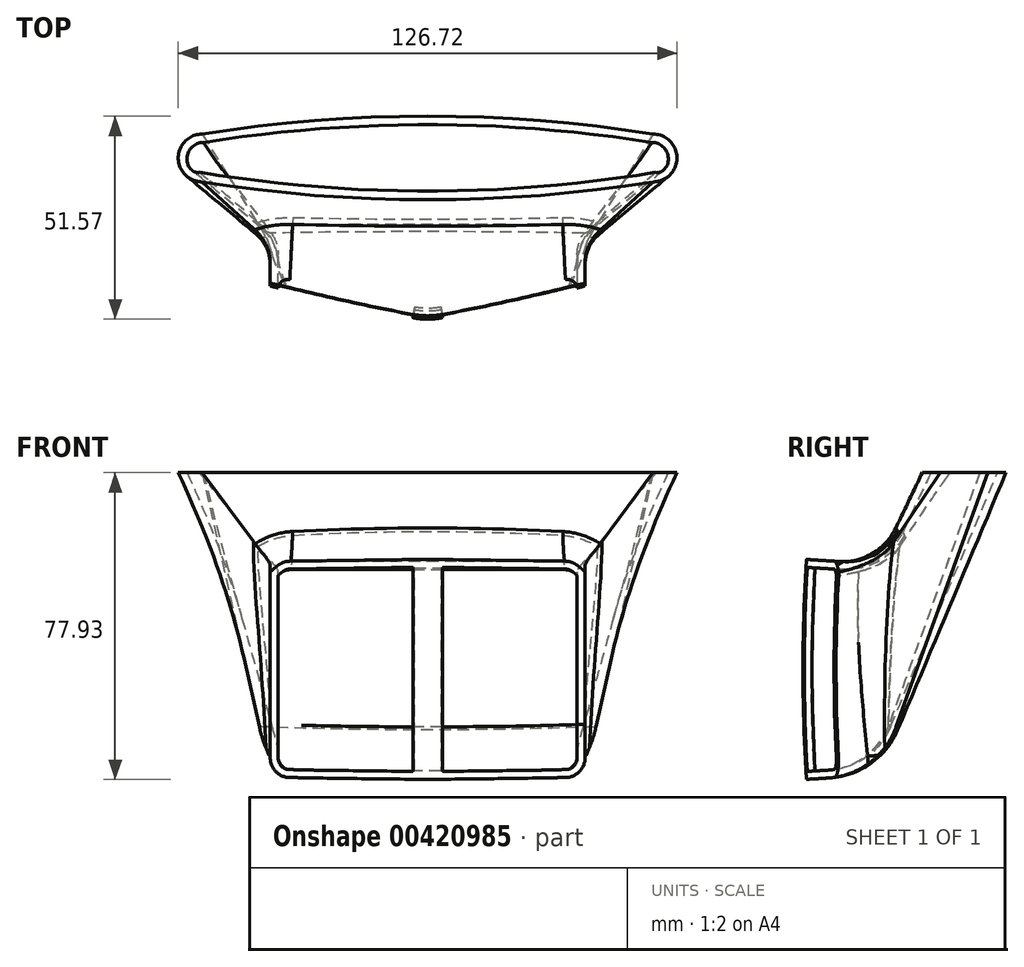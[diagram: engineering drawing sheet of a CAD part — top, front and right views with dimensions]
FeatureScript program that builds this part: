
annotation { "Feature Type Name" : "Feature", "Feature Type Description" : "" }
export const myFeature = defineFeature(function(context is Context, id is Id, definition is map)
    precondition{}
    {
        {
            var Q0;
            Q0=qCreatedBy(makeId("Top.planeOp"),FACE);
            var sketch = newSketch(context, id + "F0", { "sketchPlane" : qUnion([Q0])});
            skArc(sketch, "E0", {"start": v(-40, 0.85) * mm, "mid": v(-20.07, -3.87) * mm, "end": v(0, -7.9) * mm});
            skPoint(sketch, "E1.orphan", {"position": v(0, -7.9) * mm});
            skPoint(sketch, "E2.bottom.start.orphan", {"position": v(36.6, 0) * mm});
            skLineSegment(sketch, "E3", {"start": v(0, -7.9) * mm, "end": v(0, -4.86) * mm});
            skLineSegment(sketch, "E4.MirrorCS", {"start": v(-40, 0.85) * mm, "end": v(-40, 10.85) * mm});
            skPoint(sketch, "E5.orphan", {"position": v(40, -7.9) * mm});
            skPoint(sketch, "E6.orphan", {"position": v(74.82, 26.5) * mm});
            skPoint(sketch, "E7.orphan", {"position": v(-40, -7.9) * mm});
            skPoint(sketch, "E2.left.start.orphan", {"position": v(-36.6, 0) * mm});
            skPoint(sketch, "E8.orphan", {"position": v(-74.82, 26.5) * mm});
            skLineSegment(sketch, "E9", {"start": v(57.25, 582.23) * mm, "end": v(108.33, 582.23) * mm});
            skLineSegment(sketch, "E10.0", {"start": v(-40, 10.85) * mm, "end": v(0, 10.85) * mm});
            skPoint(sketch, "E11.orphan", {"position": v(40, 26.5) * mm});
            skPoint(sketch, "E12.0.end.orphan", {"position": v(0, 26.5) * mm});
            skPoint(sketch, "E13.orphan", {"position": v(-40, 26.5) * mm});
            skLineSegment(sketch, "E14", {"start": v(0, -4.86) * mm, "end": v(0, 10.85) * mm});
            skPoint(sketch, "E15.0.end.orphan", {"position": v(40, 10.85) * mm});
            skLineSegment(sketch, "E16.MirrorCS", {"start": v(40, 10.85) * mm, "end": v(0, 10.85) * mm});
            skLineSegment(sketch, "E17.MirrorCS", {"start": v(40, 0.85) * mm, "end": v(40, 10.85) * mm});
            skArc(sketch, "E18.MirrorCS", {"start": v(40, 0.85) * mm, "mid": v(20.07, -3.87) * mm, "end": v(0, -7.9) * mm});
            skSolve(sketch);
        }
        {
            var Q0;
            Q0=qCreatedBy(makeId("Top.planeOp"),FACE);
            var sketch = newSketch(context, id + "F1", { "sketchPlane" : qUnion([Q0])});
            skLineSegment(sketch, "E19", {"start": v(-37.76, 450) * mm, "end": v(36.32, 450) * mm});
            skSolve(sketch);
        }
        {
            var Q0;
            Q0=makeQuery(id+"F0.imprint","IMPRINT",FACE,{"disambiguationData":[TD([[makeQuery(id+"F0.imprint","IMPRINT",EDGE,{"derivedFrom":sQuery(id+"F0.wireOp",EDGE,"E3")}),-1.0]])]});
            var Q1;
            Q1=makeQuery(id+"F0.imprint","IMPRINT",FACE,{"disambiguationData":[TD([[makeQuery(id+"F0.imprint","IMPRINT",EDGE,{"derivedFrom":sQuery(id+"F0.wireOp",EDGE,"E0")}),1.0]])]});
            var Q2;
            Q2=sQuery(id+"F1.wireOp",EDGE,"E19");
            revolve(context, id + "F2", {"surfaceOperationType" : NewSurfaceOperationType.NEW, "entities" : qUnion([Q0, Q1]), "axis" : qUnion([Q2]), "revolveType" : RevolveType.SYMMETRIC, "angle" : 7 * degree});
        }
        {
            var Q0;
            Q0=makeQuery(id+"F2.opRevolve","SWEPT_EDGE",EDGE,{"disambiguationData":[OSD([sQuery(id+"F0.wireOp",EDGE,"E0"),sQuery(id+"F0.wireOp",EDGE,"E3"),sQuery(id+"F0.wireOp",EDGE,"E18.MirrorCS")])]});
            fillet(context, id + "F3", {"entities" : qUnion([Q0]), "radius" : 20 * mm, "tangentPropagation" : true, "allowEdgeOverflow" : false});
        }
        {
            var Q0;
            Q0=qCreatedBy(makeId("Top.planeOp"),FACE);
            cPlane(context, id + "F4", {"entities" : qUnion([Q0]), "cplaneType" : CPlaneType.OFFSET, "offset" : 50 * mm, "width" : 150 * mm, "height" : 150 * mm});
        }
        {
            var Q0;
            Q0=qCreatedBy(id+"F4.planeOp",FACE);
            var sketch = newSketch(context, id + "F5", { "sketchPlane" : qUnion([Q0])});
            skLineSegment(sketch, "E20.left", {"start": v(0, 27.31) * mm, "end": v(0, 27.31) * mm});
            skLineSegment(sketch, "E20.right", {"start": v(-57.28, 27.31) * mm, "end": v(-57.28, 27.31) * mm});
            skLineSegment(sketch, "E21.top", {"start": v(-57.28, 39.46) * mm, "end": v(-57.28, 39.46) * mm});
            skArc(sketch, "E22", {"start": v(57.28, 27.31) * mm, "mid": v(63.36, 33.38) * mm, "end": v(57.28, 39.46) * mm});
            skPoint(sketch, "E23.MirrorCS.end.orphan", {"position": v(57.28, 39.46) * mm});
            skArc(sketch, "E24.MirrorCS", {"start": v(-57.28, 27.31) * mm, "mid": v(-63.36, 33.38) * mm, "end": v(-57.28, 39.46) * mm});
            skPoint(sketch, "E25.MirrorCS.start.orphan", {"position": v(0, 27.31) * mm});
            skPoint(sketch, "E26.end.orphan", {"position": v(57.28, 27.31) * mm});
            skArc(sketch, "E27", {"start": v(57.28, 39.46) * mm, "mid": v(0, 44.01) * mm, "end": v(-57.28, 39.46) * mm});
            skPoint(sketch, "E28.MirrorCS.end.orphan", {"position": v(0, 39.46) * mm});
            skArc(sketch, "E29.MirrorCS", {"start": v(57.28, 27.31) * mm, "mid": v(0, 22.75) * mm, "end": v(-57.28, 27.31) * mm});
            skSolve(sketch);
        }
        {
            var Q1;
            Q1=makeQuery(id+"F5.imprint","IMPRINT",FACE,{"disambiguationData":[TD([[makeQuery(id+"F5.imprint","IMPRINT",EDGE,{"derivedFrom":sQuery(id+"F5.wireOp",EDGE,"E22")}),1.0]])]});
            var Q2;
            Q2=makeQuery(id+"F2.opRevolve","SWEPT_FACE",FACE,{"disambiguationData":[OSD([sQuery(id+"F0.wireOp",EDGE,"E10.0"),sQuery(id+"F0.wireOp",EDGE,"E16.MirrorCS")])]});
            loft(context, id + "F6", {"operationType" : NewBodyOperationType.ADD, "sheetProfilesArray" : [{ "sheetProfileEntities" : qUnion([Q1]) }, { "sheetProfileEntities" : qUnion([Q2]) }]});
        }
        {
            var Q0;
            {var subQ0=sQuery(id+"F0.wireOp",EDGE,"E17.MirrorCS");var subQ1=sQuery(id+"F0.wireOp",EDGE,"E16.MirrorCS");Q0=makeQuery(id+"F6.boolean.opBoolean","MERGE",EDGE,{"derivedFrom":[makeQuery(id+"F2.opRevolve","SWEPT_EDGE",EDGE,{"disambiguationData":[OSD([subQ1,subQ0])]}),makeQuery(id+"F6.opLoft","MID_CAP_EDGE",EDGE,{"disambiguationData":[OSD([subQ1,subQ0])],"capPos":1.0})]});}
            var Q1;
            {var subQ0=sQuery(id+"F0.wireOp",EDGE,"E10.0");var subQ1=sQuery(id+"F0.wireOp",EDGE,"E4.MirrorCS");Q1=makeQuery(id+"F6.boolean.opBoolean","MERGE",EDGE,{"derivedFrom":[makeQuery(id+"F2.opRevolve","SWEPT_EDGE",EDGE,{"disambiguationData":[OSD([subQ1,subQ0])]}),makeQuery(id+"F6.opLoft","MID_CAP_EDGE",EDGE,{"disambiguationData":[OSD([subQ1,subQ0])],"capPos":1.0})]});}
            fillet(context, id + "F7", {"entities" : qUnion([Q0, Q1]), "radius" : 10 * mm, "tangentPropagation" : true, "allowEdgeOverflow" : false});
        }
        {
            var Q0;
            {var subQ0=sQuery(id+"F0.wireOp",EDGE,"E17.MirrorCS");var subQ1=sQuery(id+"F0.wireOp",EDGE,"E16.MirrorCS");Q0=makeQuery(id+"F7.opFillet","BLEND_EDGE",EDGE,{"blendedFrom":[makeQuery(id+"F6.boolean.opBoolean","MERGE",EDGE,{"derivedFrom":[makeQuery(id+"F2.opRevolve","SWEPT_EDGE",EDGE,{"disambiguationData":[OSD([subQ1,subQ0])]}),makeQuery(id+"F6.opLoft","MID_CAP_EDGE",EDGE,{"disambiguationData":[OSD([subQ1,subQ0])],"capPos":1.0})]}),makeQuery(id+"F2.opRevolve","CAP_FACE",FACE,{"disambiguationData":[OSD([sQuery(id+"F0.wireOp",EDGE,"E0"),sQuery(id+"F0.wireOp",EDGE,"E4.MirrorCS"),sQuery(id+"F0.wireOp",EDGE,"E10.0"),subQ1,subQ0,sQuery(id+"F0.wireOp",EDGE,"E18.MirrorCS")])],"isStart":true})],"blendedInto":[makeQuery(id+"F2.opRevolve","CAP_FACE",FACE,{"disambiguationData":[OSD([sQuery(id+"F0.wireOp",EDGE,"E0"),sQuery(id+"F0.wireOp",EDGE,"E4.MirrorCS"),sQuery(id+"F0.wireOp",EDGE,"E10.0"),subQ1,subQ0,sQuery(id+"F0.wireOp",EDGE,"E18.MirrorCS")])],"isStart":true})]});}
            var Q1;
            Q1=makeQuery(id+"F2.opRevolve","CAP_EDGE",EDGE,{"disambiguationData":[OSD([sQuery(id+"F0.wireOp",EDGE,"E4.MirrorCS")])],"isStart":true});
            var Q2;
            Q2=makeQuery(id+"F2.opRevolve","CAP_EDGE",EDGE,{"disambiguationData":[OSD([sQuery(id+"F0.wireOp",EDGE,"E4.MirrorCS")])],"isStart":false});
            var Q3;
            Q3=makeQuery(id+"F2.opRevolve","CAP_EDGE",EDGE,{"disambiguationData":[OSD([sQuery(id+"F0.wireOp",EDGE,"E17.MirrorCS")])],"isStart":false});
            fillet(context, id + "F8", {"entities" : qUnion([Q0, Q1, Q2, Q3]), "radius" : 5 * mm, "tangentPropagation" : true, "allowEdgeOverflow" : false});
        }
        {
            var Q0;
            {var subQ0=sQuery(id+"F0.wireOp",EDGE,"E16.MirrorCS");var subQ1=sQuery(id+"F0.wireOp",EDGE,"E10.0");var subQ2=makeQuery(id+"F2.opRevolve","CAP_EDGE",EDGE,{"disambiguationData":[OSD([subQ1,subQ0])],"isStart":false});var subQ3=sQuery(id+"F0.wireOp",EDGE,"E17.MirrorCS");var subQ4=sQuery(id+"F0.wireOp",EDGE,"E4.MirrorCS");Q0=makeQuery(id+"F6.boolean.opBoolean","MERGE",EDGE,{"derivedFrom":[subQ2,makeQuery(id+"F6.opLoft","MID_CAP_EDGE",EDGE,{"disambiguationData":[OSD([subQ4,subQ1,subQ0,subQ3]),TDD([makeQuery(id+"F2.opRevolve","CAP_VERTEX",VERTEX,{"disambiguationData":[OSD([subQ4,subQ1])],"isStart":false}),makeQuery(id+"F2.opRevolve","CAP_VERTEX",VERTEX,{"disambiguationData":[OSD([subQ0,subQ3])],"isStart":false}),subQ2])],"capPos":1.0})]});}
            fillet(context, id + "F9", {"entities" : qUnion([Q0]), "radius" : 20 * mm, "allowEdgeOverflow" : false});
        }
        {
            var Q0;
            {var subQ0=sQuery(id+"F0.wireOp",EDGE,"E16.MirrorCS");var subQ1=sQuery(id+"F0.wireOp",EDGE,"E10.0");var subQ2=makeQuery(id+"F2.opRevolve","CAP_EDGE",EDGE,{"disambiguationData":[OSD([subQ1,subQ0])],"isStart":true});var subQ3=sQuery(id+"F0.wireOp",EDGE,"E17.MirrorCS");var subQ4=sQuery(id+"F0.wireOp",EDGE,"E4.MirrorCS");Q0=makeQuery(id+"F6.boolean.opBoolean","MERGE",EDGE,{"derivedFrom":[subQ2,makeQuery(id+"F6.opLoft","MID_CAP_EDGE",EDGE,{"disambiguationData":[OSD([subQ4,subQ1,subQ0,subQ3]),TDD([makeQuery(id+"F2.opRevolve","CAP_VERTEX",VERTEX,{"disambiguationData":[OSD([subQ4,subQ1])],"isStart":true}),makeQuery(id+"F2.opRevolve","CAP_VERTEX",VERTEX,{"disambiguationData":[OSD([subQ0,subQ3])],"isStart":true}),subQ2])],"capPos":1.0})]});}
            var Q1;
            {var subQ0=sQuery(id+"F0.wireOp",EDGE,"E17.MirrorCS");var subQ1=sQuery(id+"F0.wireOp",EDGE,"E16.MirrorCS");var subQ2=sQuery(id+"F0.wireOp",EDGE,"E10.0");var subQ3=sQuery(id+"F0.wireOp",EDGE,"E4.MirrorCS");Q1=makeQuery(id+"F8.opFillet","BLEND_EDGE",EDGE,{"blendedFrom":[makeQuery(id+"F7.opFillet","BLEND_EDGE",EDGE,{"blendedFrom":[makeQuery(id+"F6.boolean.opBoolean","MERGE",EDGE,{"derivedFrom":[makeQuery(id+"F2.opRevolve","SWEPT_EDGE",EDGE,{"disambiguationData":[OSD([subQ3,subQ2])]}),makeQuery(id+"F6.opLoft","MID_CAP_EDGE",EDGE,{"disambiguationData":[OSD([subQ3,subQ2])],"capPos":1.0})]}),makeQuery(id+"F2.opRevolve","CAP_FACE",FACE,{"disambiguationData":[OSD([sQuery(id+"F0.wireOp",EDGE,"E0"),subQ3,subQ2,subQ1,subQ0,sQuery(id+"F0.wireOp",EDGE,"E18.MirrorCS")])],"isStart":true})],"blendedInto":[makeQuery(id+"F2.opRevolve","CAP_FACE",FACE,{"disambiguationData":[OSD([sQuery(id+"F0.wireOp",EDGE,"E0"),subQ3,subQ2,subQ1,subQ0,sQuery(id+"F0.wireOp",EDGE,"E18.MirrorCS")])],"isStart":true})]}),makeQuery(id+"F6.opLoft","SWEPT_FACE",FACE,{"disambiguationData":[OSD([subQ3,subQ2,subQ1,subQ0,sQuery(id+"F5.wireOp",EDGE,"E22"),sQuery(id+"F5.wireOp",EDGE,"E24.MirrorCS"),sQuery(id+"F5.wireOp",EDGE,"E29.MirrorCS")])]})],"blendedInto":[makeQuery(id+"F6.opLoft","SWEPT_FACE",FACE,{"disambiguationData":[OSD([subQ3,subQ2,subQ1,subQ0,sQuery(id+"F5.wireOp",EDGE,"E22"),sQuery(id+"F5.wireOp",EDGE,"E24.MirrorCS"),sQuery(id+"F5.wireOp",EDGE,"E29.MirrorCS")])]})]});}
            var Q2;
            {var subQ0=sQuery(id+"F0.wireOp",EDGE,"E17.MirrorCS");var subQ1=sQuery(id+"F0.wireOp",EDGE,"E16.MirrorCS");var subQ2=sQuery(id+"F0.wireOp",EDGE,"E10.0");var subQ3=sQuery(id+"F0.wireOp",EDGE,"E4.MirrorCS");Q2=makeQuery(id+"F8.opFillet","BLEND_EDGE",EDGE,{"blendedFrom":[makeQuery(id+"F7.opFillet","BLEND_EDGE",EDGE,{"blendedFrom":[makeQuery(id+"F6.boolean.opBoolean","MERGE",EDGE,{"derivedFrom":[makeQuery(id+"F2.opRevolve","SWEPT_EDGE",EDGE,{"disambiguationData":[OSD([subQ1,subQ0])]}),makeQuery(id+"F6.opLoft","MID_CAP_EDGE",EDGE,{"disambiguationData":[OSD([subQ1,subQ0])],"capPos":1.0})]}),makeQuery(id+"F2.opRevolve","CAP_FACE",FACE,{"disambiguationData":[OSD([sQuery(id+"F0.wireOp",EDGE,"E0"),subQ3,subQ2,subQ1,subQ0,sQuery(id+"F0.wireOp",EDGE,"E18.MirrorCS")])],"isStart":true})],"blendedInto":[makeQuery(id+"F2.opRevolve","CAP_FACE",FACE,{"disambiguationData":[OSD([sQuery(id+"F0.wireOp",EDGE,"E0"),subQ3,subQ2,subQ1,subQ0,sQuery(id+"F0.wireOp",EDGE,"E18.MirrorCS")])],"isStart":true})]}),makeQuery(id+"F6.opLoft","SWEPT_FACE",FACE,{"disambiguationData":[OSD([subQ3,subQ2,subQ1,subQ0,sQuery(id+"F5.wireOp",EDGE,"E22"),sQuery(id+"F5.wireOp",EDGE,"E24.MirrorCS"),sQuery(id+"F5.wireOp",EDGE,"E29.MirrorCS")])]})],"blendedInto":[makeQuery(id+"F6.opLoft","SWEPT_FACE",FACE,{"disambiguationData":[OSD([subQ3,subQ2,subQ1,subQ0,sQuery(id+"F5.wireOp",EDGE,"E22"),sQuery(id+"F5.wireOp",EDGE,"E24.MirrorCS"),sQuery(id+"F5.wireOp",EDGE,"E29.MirrorCS")])]})]});}
            fillet(context, id + "F10", {"entities" : qUnion([Q0, Q1, Q2]), "radius" : 15 * mm, "tangentPropagation" : true, "allowEdgeOverflow" : false});
        }
        {
            var Q0;
            Q0=makeQuery(id+"F6.opLoft","CAP_FACE",FACE,{"disambiguationData":[OSD([makeQuery(id+"F5.imprint","IMPRINT",FACE,{"disambiguationData":[TD([[makeQuery(id+"F5.imprint","IMPRINT",EDGE,{"derivedFrom":sQuery(id+"F5.wireOp",EDGE,"E22")}),1.0]])]})])],"isStart":true});
            var Q1;
            Q1=makeQuery(id+"F2.opRevolve","SWEPT_FACE",FACE,{"disambiguationData":[OSD([sQuery(id+"F0.wireOp",EDGE,"E0")])]});
            var Q2;
            Q2=makeQuery(id+"F2.opRevolve","SWEPT_FACE",FACE,{"disambiguationData":[OSD([sQuery(id+"F0.wireOp",EDGE,"E18.MirrorCS")])]});
            shell(context, id + "F11", {"entities" : qUnion([Q0, Q1, Q2]), "thickness" : 2 * mm});
        }
    });
